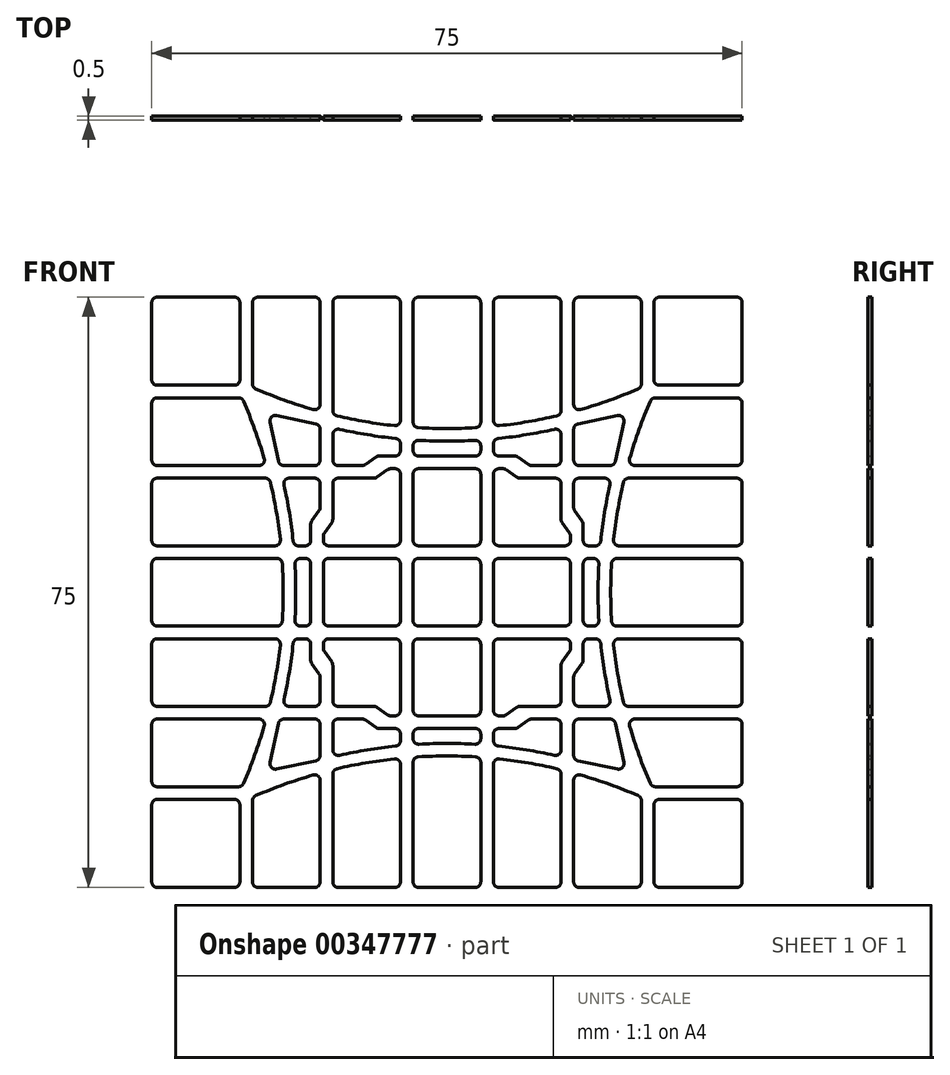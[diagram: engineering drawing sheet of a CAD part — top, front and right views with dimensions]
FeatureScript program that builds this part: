
annotation { "Feature Type Name" : "Feature", "Feature Type Description" : "" }
export const myFeature = defineFeature(function(context is Context, id is Id, definition is map)
    precondition{}
    {
        {
            var Q0;
            Q0=qCreatedBy(makeId("Front.planeOp"),FACE);
            var sketch = newSketch(context, id + "F0", { "sketchPlane" : qUnion([Q0])});
            skLineSegment(sketch, "E0.bottom", {"start": v(39, 39) * mm, "end": v(-39, 39) * mm, "construction": true});
            skLineSegment(sketch, "E0.top", {"start": v(39, -39) * mm, "end": v(-39, -39) * mm, "construction": true});
            skLineSegment(sketch, "E0.left", {"start": v(39, 39) * mm, "end": v(39, -39) * mm, "construction": true});
            skLineSegment(sketch, "E0.right", {"start": v(-39, 39) * mm, "end": v(-39, -39) * mm, "construction": true});
            skPoint(sketch, "E0.middle", {"position": v(0, 0) * mm});
            skLineSegment(sketch, "E1", {"start": v(-39, -25.5) * mm, "end": v(39, -25.5) * mm, "construction": true});
            skLineSegment(sketch, "E2", {"start": v(-39, -39) * mm, "end": v(0, 0) * mm, "construction": true});
            skLineSegment(sketch, "E3", {"start": v(39, -39) * mm, "end": v(0, 0) * mm, "construction": true});
            skPoint(sketch, "E4", {"position": v(-25.5, -25.5) * mm});
            skPoint(sketch, "E5", {"position": v(25.5, -25.5) * mm});
            skLineSegment(sketch, "E6", {"start": v(0, 0) * mm, "end": v(0, -39) * mm, "construction": true});
            skArc(sketch, "E7", {"start": v(25.5, -25.5) * mm, "mid": v(0, -20) * mm, "end": v(-25.5, -25.5) * mm, "construction": true});
            skLineSegment(sketch, "E8", {"start": v(-25.5, -25.5) * mm, "end": v(-25.5, -39) * mm, "construction": true});
            skLineSegment(sketch, "E9", {"start": v(-15.3, -25.5) * mm, "end": v(-15.3, -39) * mm, "construction": true});
            skLineSegment(sketch, "E10", {"start": v(-5.1, -25.5) * mm, "end": v(-5.1, -39) * mm, "construction": true});
            skLineSegment(sketch, "E11.MirrorCS", {"start": v(5.1, -25.5) * mm, "end": v(5.1, -39) * mm, "construction": true});
            skLineSegment(sketch, "E12.MirrorCS", {"start": v(15.3, -25.5) * mm, "end": v(15.3, -39) * mm, "construction": true});
            skLineSegment(sketch, "E13.MirrorCS", {"start": v(25.5, -25.5) * mm, "end": v(25.5, -39) * mm, "construction": true});
            skLineSegment(sketch, "E14", {"start": v(-15.3, -25.5) * mm, "end": v(-15.3, -21.92) * mm, "construction": true});
            skLineSegment(sketch, "E15", {"start": v(-5.1, -25.5) * mm, "end": v(-5.1, -20.21) * mm, "construction": true});
            skLineSegment(sketch, "E16.MirrorCS", {"start": v(5.1, -25.5) * mm, "end": v(5.1, -20.21) * mm, "construction": true});
            skLineSegment(sketch, "E17.MirrorCS", {"start": v(15.3, -25.5) * mm, "end": v(15.3, -21.92) * mm, "construction": true});
            skLineSegment(sketch, "E18", {"start": v(-15.3, -21.92) * mm, "end": v(-15.3, -15.3) * mm, "construction": true});
            skLineSegment(sketch, "E19", {"start": v(-5.1, -20.21) * mm, "end": v(-5.1, -5.1) * mm, "construction": true});
            skLineSegment(sketch, "E20", {"start": v(5.1, -20.21) * mm, "end": v(5.1, -5.1) * mm, "construction": true});
            skLineSegment(sketch, "E21", {"start": v(5.1, -5.1) * mm, "end": v(-5.1, -5.1) * mm, "construction": true});
            skLineSegment(sketch, "E22", {"start": v(-5.1, -16.5) * mm, "end": v(5.1, -16.5) * mm, "construction": true});
            skLineSegment(sketch, "E23", {"start": v(-15.3, -15.3) * mm, "end": v(-9.3, -15.3) * mm, "construction": true});
            skLineSegment(sketch, "E24", {"start": v(-9.3, -15.3) * mm, "end": v(-7.6, -16.5) * mm, "construction": true});
            skLineSegment(sketch, "E25", {"start": v(-7.6, -16.5) * mm, "end": v(-5.1, -16.5) * mm, "construction": true});
            skLineSegment(sketch, "E26", {"start": v(-10.3, -15.3) * mm, "end": v(-8.6, -16.5) * mm, "construction": true});
            skLineSegment(sketch, "E27", {"start": v(-8.6, -16.5) * mm, "end": v(-7.6, -16.5) * mm, "construction": true});
            skArc(sketch, "E28.MirrorCS", {"start": v(-25.5, 25.5) * mm, "mid": v(-20, 0) * mm, "end": v(-25.5, -25.5) * mm, "construction": true});
            skLineSegment(sketch, "E29.MirrorCS", {"start": v(-15.3, -15.3) * mm, "end": v(-15.3, -9.3) * mm, "construction": true});
            skLineSegment(sketch, "E30.MirrorCS", {"start": v(-15.3, -10.3) * mm, "end": v(-16.5, -8.6) * mm, "construction": true});
            skLineSegment(sketch, "E31.MirrorCS", {"start": v(-15.3, -9.3) * mm, "end": v(-16.5, -7.6) * mm, "construction": true});
            skLineSegment(sketch, "E32.MirrorCS", {"start": v(-16.5, -8.6) * mm, "end": v(-16.5, -7.6) * mm, "construction": true});
            skLineSegment(sketch, "E33.MirrorCS", {"start": v(-16.5, -7.6) * mm, "end": v(-16.5, -5.1) * mm, "construction": true});
            skLineSegment(sketch, "E34.MirrorCS", {"start": v(-20.21, -5.1) * mm, "end": v(-5.1, -5.1) * mm, "construction": true});
            skLineSegment(sketch, "E35.MirrorCS", {"start": v(-21.92, -15.3) * mm, "end": v(-15.3, -15.3) * mm, "construction": true});
            skLineSegment(sketch, "E36", {"start": v(-21.92, -15.3) * mm, "end": v(-23.73, -23.73) * mm, "construction": true});
            skLineSegment(sketch, "E37", {"start": v(-23.73, -23.73) * mm, "end": v(-15.3, -21.92) * mm, "construction": true});
            skLineSegment(sketch, "E38.bottom", {"start": v(-3.6, -4.3) * mm, "end": v(3.6, -4.3) * mm});
            skLineSegment(sketch, "E38.top", {"start": v(-3.6, 4.3) * mm, "end": v(3.6, 4.3) * mm});
            skLineSegment(sketch, "E38.left", {"start": v(-4.3, -3.6) * mm, "end": v(-4.3, 3.6) * mm});
            skLineSegment(sketch, "E38.right", {"start": v(4.3, -3.6) * mm, "end": v(4.3, 3.6) * mm});
            skLineSegment(sketch, "E39.bottom", {"start": v(-3.6, -5.9) * mm, "end": v(3.6, -5.9) * mm});
            skLineSegment(sketch, "E39.top", {"start": v(-3.6, -15.7) * mm, "end": v(3.6, -15.7) * mm});
            skLineSegment(sketch, "E39.left", {"start": v(-4.3, -6.6) * mm, "end": v(-4.3, -15) * mm});
            skLineSegment(sketch, "E39.right", {"start": v(4.3, -6.6) * mm, "end": v(4.3, -15) * mm});
            skLineSegment(sketch, "E40.bottom", {"start": v(-36.8, -26.3) * mm, "end": v(-27, -26.3) * mm});
            skLineSegment(sketch, "E40.top", {"start": v(-36.8, -37.5) * mm, "end": v(-27, -37.5) * mm});
            skLineSegment(sketch, "E40.left", {"start": v(-37.5, -27) * mm, "end": v(-37.5, -36.8) * mm});
            skLineSegment(sketch, "E40.right", {"start": v(-26.3, -27) * mm, "end": v(-26.3, -36.8) * mm});
            skArc(sketch, "E41.0", {"start": v(25.83, -24.77) * mm, "mid": v(0, -19.2) * mm, "end": v(-25.83, -24.77) * mm, "construction": true});
            skArc(sketch, "E42.0", {"start": v(25.17, -26.23) * mm, "mid": v(0, -20.8) * mm, "end": v(-25.17, -26.23) * mm, "construction": true});
            skLineSegment(sketch, "E43", {"start": v(-4.3, -18.6) * mm, "end": v(-4.3, -18) * mm});
            skLineSegment(sketch, "E44", {"start": v(-3.6, -17.3) * mm, "end": v(3.6, -17.3) * mm});
            skLineSegment(sketch, "E45", {"start": v(4.3, -18) * mm, "end": v(4.3, -18.6) * mm});
            skArc(sketch, "E46", {"start": v(3.56, -19.3) * mm, "mid": v(0, -19.2) * mm, "end": v(-3.56, -19.3) * mm});
            skLineSegment(sketch, "E47", {"start": v(-4.3, -21.6) * mm, "end": v(-4.3, -36.8) * mm});
            skLineSegment(sketch, "E48", {"start": v(-3.6, -37.5) * mm, "end": v(3.6, -37.5) * mm});
            skLineSegment(sketch, "E49", {"start": v(4.3, -36.8) * mm, "end": v(4.3, -21.6) * mm});
            skArc(sketch, "E50", {"start": v(3.64, -20.9) * mm, "mid": v(0, -20.8) * mm, "end": v(-3.64, -20.9) * mm});
            skLineSegment(sketch, "E51", {"start": v(-24.7, -26.48) * mm, "end": v(-24.7, -36.8) * mm});
            skLineSegment(sketch, "E52", {"start": v(-24, -37.5) * mm, "end": v(-16.8, -37.5) * mm});
            skLineSegment(sketch, "E53", {"start": v(-16.1, -36.8) * mm, "end": v(-16.1, -23.88) * mm});
            skArc(sketch, "E54", {"start": v(-17, -23.21) * mm, "mid": v(-20.68, -24.4) * mm, "end": v(-24.28, -25.83) * mm});
            skLineSegment(sketch, "E55", {"start": v(-14.5, -23.1) * mm, "end": v(-14.5, -36.8) * mm});
            skLineSegment(sketch, "E56", {"start": v(-13.8, -37.5) * mm, "end": v(-6.6, -37.5) * mm});
            skLineSegment(sketch, "E57", {"start": v(-5.9, -36.8) * mm, "end": v(-5.9, -21.86) * mm});
            skArc(sketch, "E58", {"start": v(-6.68, -21.17) * mm, "mid": v(-10.34, -21.68) * mm, "end": v(-13.96, -22.42) * mm});
            skLineSegment(sketch, "E59", {"start": v(-16.1, -16.8) * mm, "end": v(-16.1, -20.7) * mm});
            skLineSegment(sketch, "E60", {"start": v(-16.65, -21.4) * mm, "end": v(-21.63, -22.46) * mm});
            skLineSegment(sketch, "E61.MirrorCS", {"start": v(-21.4, -16.65) * mm, "end": v(-22.46, -21.63) * mm});
            skLineSegment(sketch, "E62.MirrorCS", {"start": v(-16.8, -16.1) * mm, "end": v(-20.7, -16.1) * mm});
            skLineSegment(sketch, "E63", {"start": v(-14.5, -20.02) * mm, "end": v(-14.5, -16.8) * mm});
            skLineSegment(sketch, "E64", {"start": v(-13.8, -16.1) * mm, "end": v(-10.78, -16.1) * mm});
            skLineSegment(sketch, "E65", {"start": v(-10.37, -16.23) * mm, "end": v(-9.04, -17.17) * mm});
            skLineSegment(sketch, "E66", {"start": v(-8.63, -17.3) * mm, "end": v(-6.6, -17.3) * mm});
            skLineSegment(sketch, "E67", {"start": v(-5.9, -18) * mm, "end": v(-5.9, -18.84) * mm});
            skArc(sketch, "E68", {"start": v(-6.53, -19.54) * mm, "mid": v(-10.1, -20.02) * mm, "end": v(-13.65, -20.7) * mm});
            skLineSegment(sketch, "E69", {"start": v(-5.9, -6.6) * mm, "end": v(-5.9, -15) * mm});
            skLineSegment(sketch, "E70", {"start": v(-6.6, -15.7) * mm, "end": v(-7.12, -15.7) * mm});
            skLineSegment(sketch, "E71", {"start": v(-7.53, -15.57) * mm, "end": v(-8.86, -14.63) * mm});
            skLineSegment(sketch, "E72", {"start": v(-9.27, -14.5) * mm, "end": v(-13.8, -14.5) * mm});
            skLineSegment(sketch, "E73.MirrorCS", {"start": v(-6.6, -5.9) * mm, "end": v(-15, -5.9) * mm});
            skLineSegment(sketch, "E74.MirrorCS", {"start": v(-15.7, -6.6) * mm, "end": v(-15.7, -7.12) * mm});
            skLineSegment(sketch, "E75.MirrorCS", {"start": v(-15.57, -7.53) * mm, "end": v(-14.63, -8.86) * mm});
            skLineSegment(sketch, "E76.MirrorCS", {"start": v(-14.5, -9.27) * mm, "end": v(-14.5, -13.8) * mm});
            skPoint(sketch, "E77.visualSharp", {"position": v(-37.5, -26.3) * mm});
            skArc(sketch, "E77.filletArc", {"start": v(-36.8, -26.3) * mm, "mid": v(-37.3, -26.5) * mm, "end": v(-37.5, -27) * mm});
            skPoint(sketch, "E78.visualSharp", {"position": v(-26.3, -26.3) * mm});
            skArc(sketch, "E78.filletArc", {"start": v(-26.3, -27) * mm, "mid": v(-26.5, -26.5) * mm, "end": v(-27, -26.3) * mm});
            skPoint(sketch, "E79.visualSharp", {"position": v(-26.3, -37.5) * mm});
            skArc(sketch, "E79.filletArc", {"start": v(-27, -37.5) * mm, "mid": v(-26.5, -37.3) * mm, "end": v(-26.3, -36.8) * mm});
            skPoint(sketch, "E80.visualSharp", {"position": v(-37.5, -37.5) * mm});
            skArc(sketch, "E80.filletArc", {"start": v(-37.5, -36.8) * mm, "mid": v(-37.3, -37.3) * mm, "end": v(-36.8, -37.5) * mm});
            skPoint(sketch, "E81.visualSharp", {"position": v(-24.7, -37.5) * mm});
            skArc(sketch, "E81.filletArc", {"start": v(-24.7, -36.8) * mm, "mid": v(-24.5, -37.3) * mm, "end": v(-24, -37.5) * mm});
            skPoint(sketch, "E82.visualSharp", {"position": v(-24.7, -26.02) * mm});
            skArc(sketch, "E82.filletArc", {"start": v(-24.28, -25.83) * mm, "mid": v(-24.59, -26.1) * mm, "end": v(-24.7, -26.48) * mm});
            skPoint(sketch, "E83.visualSharp", {"position": v(-16.1, -22.96) * mm});
            skArc(sketch, "E83.filletArc", {"start": v(-16.1, -23.88) * mm, "mid": v(-16.38, -23.33) * mm, "end": v(-17, -23.21) * mm});
            skPoint(sketch, "E84.visualSharp", {"position": v(-16.1, -37.5) * mm});
            skArc(sketch, "E84.filletArc", {"start": v(-16.8, -37.5) * mm, "mid": v(-16.3, -37.3) * mm, "end": v(-16.1, -36.8) * mm});
            skPoint(sketch, "E85.visualSharp", {"position": v(-14.5, -37.5) * mm});
            skArc(sketch, "E85.filletArc", {"start": v(-14.5, -36.8) * mm, "mid": v(-14.3, -37.3) * mm, "end": v(-13.8, -37.5) * mm});
            skPoint(sketch, "E86.visualSharp", {"position": v(-5.9, -37.5) * mm});
            skArc(sketch, "E86.filletArc", {"start": v(-6.6, -37.5) * mm, "mid": v(-6.1, -37.3) * mm, "end": v(-5.9, -36.8) * mm});
            skPoint(sketch, "E87.visualSharp", {"position": v(-5.9, -21.09) * mm});
            skArc(sketch, "E87.filletArc", {"start": v(-5.9, -21.86) * mm, "mid": v(-6.13, -21.34) * mm, "end": v(-6.68, -21.17) * mm});
            skPoint(sketch, "E88.visualSharp", {"position": v(-14.5, -22.55) * mm});
            skArc(sketch, "E88.filletArc", {"start": v(-13.96, -22.42) * mm, "mid": v(-14.35, -22.66) * mm, "end": v(-14.5, -23.1) * mm});
            skPoint(sketch, "E89.visualSharp", {"position": v(-4.3, -37.5) * mm});
            skArc(sketch, "E89.filletArc", {"start": v(-4.3, -36.8) * mm, "mid": v(-4.1, -37.3) * mm, "end": v(-3.6, -37.5) * mm});
            skPoint(sketch, "E90.visualSharp", {"position": v(4.3, -37.5) * mm});
            skArc(sketch, "E90.filletArc", {"start": v(3.6, -37.5) * mm, "mid": v(4.1, -37.3) * mm, "end": v(4.3, -36.8) * mm});
            skPoint(sketch, "E91.visualSharp", {"position": v(4.3, -20.95) * mm});
            skArc(sketch, "E91.filletArc", {"start": v(4.3, -21.6) * mm, "mid": v(4.1, -21.13) * mm, "end": v(3.64, -20.9) * mm});
            skPoint(sketch, "E92.visualSharp", {"position": v(-4.3, -20.95) * mm});
            skArc(sketch, "E92.filletArc", {"start": v(-3.64, -20.9) * mm, "mid": v(-4.1, -21.13) * mm, "end": v(-4.3, -21.6) * mm});
            skPoint(sketch, "E93.visualSharp", {"position": v(-4.3, -17.3) * mm});
            skArc(sketch, "E93.filletArc", {"start": v(-3.6, -17.3) * mm, "mid": v(-4.1, -17.5) * mm, "end": v(-4.3, -18) * mm});
            skPoint(sketch, "E94.visualSharp", {"position": v(4.3, -17.3) * mm});
            skArc(sketch, "E94.filletArc", {"start": v(4.3, -18) * mm, "mid": v(4.1, -17.5) * mm, "end": v(3.6, -17.3) * mm});
            skPoint(sketch, "E95.visualSharp", {"position": v(-4.3, -19.35) * mm});
            skArc(sketch, "E95.filletArc", {"start": v(-4.3, -18.6) * mm, "mid": v(-4.08, -19.11) * mm, "end": v(-3.56, -19.3) * mm});
            skPoint(sketch, "E96.visualSharp", {"position": v(4.3, -19.35) * mm});
            skArc(sketch, "E96.filletArc", {"start": v(3.56, -19.3) * mm, "mid": v(4.08, -19.11) * mm, "end": v(4.3, -18.6) * mm});
            skPoint(sketch, "E97.visualSharp", {"position": v(-14.5, -16.1) * mm});
            skArc(sketch, "E97.filletArc", {"start": v(-13.8, -16.1) * mm, "mid": v(-14.3, -16.3) * mm, "end": v(-14.5, -16.8) * mm});
            skPoint(sketch, "E98.visualSharp", {"position": v(-10.55, -16.1) * mm});
            skArc(sketch, "E98.filletArc", {"start": v(-10.37, -16.23) * mm, "mid": v(-10.56, -16.13) * mm, "end": v(-10.78, -16.1) * mm});
            skPoint(sketch, "E99.visualSharp", {"position": v(-8.85, -17.3) * mm});
            skArc(sketch, "E99.filletArc", {"start": v(-9.04, -17.17) * mm, "mid": v(-8.84, -17.27) * mm, "end": v(-8.63, -17.3) * mm});
            skPoint(sketch, "E100.visualSharp", {"position": v(-5.9, -17.3) * mm});
            skArc(sketch, "E100.filletArc", {"start": v(-5.9, -18) * mm, "mid": v(-6.1, -17.5) * mm, "end": v(-6.6, -17.3) * mm});
            skPoint(sketch, "E101.visualSharp", {"position": v(-5.9, -19.48) * mm});
            skArc(sketch, "E101.filletArc", {"start": v(-6.53, -19.54) * mm, "mid": v(-6.08, -19.31) * mm, "end": v(-5.9, -18.84) * mm});
            skPoint(sketch, "E102.visualSharp", {"position": v(-14.5, -20.9) * mm});
            skArc(sketch, "E102.filletArc", {"start": v(-14.5, -20.02) * mm, "mid": v(-14.24, -20.57) * mm, "end": v(-13.65, -20.7) * mm});
            skPoint(sketch, "E103.visualSharp", {"position": v(-21.28, -16.1) * mm});
            skArc(sketch, "E103.filletArc", {"start": v(-20.7, -16.1) * mm, "mid": v(-21.15, -16.26) * mm, "end": v(-21.4, -16.65) * mm});
            skPoint(sketch, "E104.visualSharp", {"position": v(-16.1, -16.1) * mm});
            skArc(sketch, "E104.filletArc", {"start": v(-16.1, -16.8) * mm, "mid": v(-16.3, -16.3) * mm, "end": v(-16.8, -16.1) * mm});
            skPoint(sketch, "E105.visualSharp", {"position": v(-16.1, -21.28) * mm});
            skArc(sketch, "E105.filletArc", {"start": v(-16.65, -21.4) * mm, "mid": v(-16.26, -21.15) * mm, "end": v(-16.1, -20.7) * mm});
            skPoint(sketch, "E106.visualSharp", {"position": v(-22.7, -22.7) * mm});
            skArc(sketch, "E106.filletArc", {"start": v(-22.46, -21.63) * mm, "mid": v(-22.27, -22.27) * mm, "end": v(-21.63, -22.46) * mm});
            skPoint(sketch, "E107.visualSharp", {"position": v(-14.5, -14.5) * mm});
            skArc(sketch, "E107.filletArc", {"start": v(-14.5, -13.8) * mm, "mid": v(-14.3, -14.3) * mm, "end": v(-13.8, -14.5) * mm});
            skPoint(sketch, "E108.visualSharp", {"position": v(-9.05, -14.5) * mm});
            skArc(sketch, "E108.filletArc", {"start": v(-8.86, -14.63) * mm, "mid": v(-9.06, -14.53) * mm, "end": v(-9.27, -14.5) * mm});
            skPoint(sketch, "E109.visualSharp", {"position": v(-7.35, -15.7) * mm});
            skArc(sketch, "E109.filletArc", {"start": v(-7.53, -15.57) * mm, "mid": v(-7.34, -15.67) * mm, "end": v(-7.12, -15.7) * mm});
            skPoint(sketch, "E110.visualSharp", {"position": v(-5.9, -15.7) * mm});
            skArc(sketch, "E110.filletArc", {"start": v(-6.6, -15.7) * mm, "mid": v(-6.1, -15.5) * mm, "end": v(-5.9, -15) * mm});
            skPoint(sketch, "E111.visualSharp", {"position": v(-5.9, -5.9) * mm});
            skArc(sketch, "E111.filletArc", {"start": v(-5.9, -6.6) * mm, "mid": v(-6.1, -6.1) * mm, "end": v(-6.6, -5.9) * mm});
            skPoint(sketch, "E112.visualSharp", {"position": v(-15.7, -5.9) * mm});
            skArc(sketch, "E112.filletArc", {"start": v(-15, -5.9) * mm, "mid": v(-15.5, -6.1) * mm, "end": v(-15.7, -6.6) * mm});
            skPoint(sketch, "E113.visualSharp", {"position": v(-14.5, -9.05) * mm});
            skArc(sketch, "E113.filletArc", {"start": v(-14.5, -9.27) * mm, "mid": v(-14.53, -9.06) * mm, "end": v(-14.63, -8.86) * mm});
            skPoint(sketch, "E114.visualSharp", {"position": v(-15.7, -7.35) * mm});
            skArc(sketch, "E114.filletArc", {"start": v(-15.7, -7.12) * mm, "mid": v(-15.67, -7.34) * mm, "end": v(-15.57, -7.53) * mm});
            skPoint(sketch, "E115.visualSharp", {"position": v(-4.3, -5.9) * mm});
            skArc(sketch, "E115.filletArc", {"start": v(-3.6, -5.9) * mm, "mid": v(-4.1, -6.1) * mm, "end": v(-4.3, -6.6) * mm});
            skPoint(sketch, "E116.visualSharp", {"position": v(-4.3, -15.7) * mm});
            skArc(sketch, "E116.filletArc", {"start": v(-4.3, -15) * mm, "mid": v(-4.1, -15.5) * mm, "end": v(-3.6, -15.7) * mm});
            skPoint(sketch, "E117.visualSharp", {"position": v(4.3, -15.7) * mm});
            skArc(sketch, "E117.filletArc", {"start": v(3.6, -15.7) * mm, "mid": v(4.1, -15.5) * mm, "end": v(4.3, -15) * mm});
            skPoint(sketch, "E118.visualSharp", {"position": v(4.3, -5.9) * mm});
            skArc(sketch, "E118.filletArc", {"start": v(4.3, -6.6) * mm, "mid": v(4.1, -6.1) * mm, "end": v(3.6, -5.9) * mm});
            skPoint(sketch, "E119.visualSharp", {"position": v(-4.3, 4.3) * mm});
            skArc(sketch, "E119.filletArc", {"start": v(-3.6, 4.3) * mm, "mid": v(-4.1, 4.1) * mm, "end": v(-4.3, 3.6) * mm});
            skPoint(sketch, "E120.visualSharp", {"position": v(-4.3, -4.3) * mm});
            skArc(sketch, "E120.filletArc", {"start": v(-4.3, -3.6) * mm, "mid": v(-4.1, -4.1) * mm, "end": v(-3.6, -4.3) * mm});
            skPoint(sketch, "E121.visualSharp", {"position": v(4.3, -4.3) * mm});
            skArc(sketch, "E121.filletArc", {"start": v(3.6, -4.3) * mm, "mid": v(4.1, -4.1) * mm, "end": v(4.3, -3.6) * mm});
            skPoint(sketch, "E122.visualSharp", {"position": v(4.3, 4.3) * mm});
            skArc(sketch, "E122.filletArc", {"start": v(4.3, 3.6) * mm, "mid": v(4.1, 4.1) * mm, "end": v(3.6, 4.3) * mm});
            skLineSegment(sketch, "E123.MirrorCS", {"start": v(8.63, -17.3) * mm, "end": v(6.6, -17.3) * mm});
            skArc(sketch, "E124.MirrorCS", {"start": v(5.9, -18) * mm, "mid": v(6.1, -17.5) * mm, "end": v(6.6, -17.3) * mm});
            skLineSegment(sketch, "E125.MirrorCS", {"start": v(5.9, -18) * mm, "end": v(5.9, -18.84) * mm});
            skArc(sketch, "E126.MirrorCS", {"start": v(6.53, -19.54) * mm, "mid": v(6.08, -19.31) * mm, "end": v(5.9, -18.84) * mm});
            skArc(sketch, "E127.MirrorCS", {"start": v(6.53, -19.54) * mm, "mid": v(10.1, -20.02) * mm, "end": v(13.65, -20.7) * mm});
            skArc(sketch, "E128.MirrorCS", {"start": v(14.5, -20.02) * mm, "mid": v(14.24, -20.57) * mm, "end": v(13.65, -20.7) * mm});
            skLineSegment(sketch, "E129.MirrorCS", {"start": v(14.5, -20.02) * mm, "end": v(14.5, -16.8) * mm});
            skArc(sketch, "E130.MirrorCS", {"start": v(13.8, -16.1) * mm, "mid": v(14.3, -16.3) * mm, "end": v(14.5, -16.8) * mm});
            skLineSegment(sketch, "E131.MirrorCS", {"start": v(13.8, -16.1) * mm, "end": v(10.78, -16.1) * mm});
            skArc(sketch, "E132.MirrorCS", {"start": v(10.37, -16.23) * mm, "mid": v(10.56, -16.13) * mm, "end": v(10.78, -16.1) * mm});
            skLineSegment(sketch, "E133.MirrorCS", {"start": v(10.37, -16.23) * mm, "end": v(9.04, -17.17) * mm});
            skArc(sketch, "E134.MirrorCS", {"start": v(9.04, -17.17) * mm, "mid": v(8.84, -17.27) * mm, "end": v(8.63, -17.3) * mm});
            skLineSegment(sketch, "E135.MirrorCS", {"start": v(5.9, -36.8) * mm, "end": v(5.9, -21.86) * mm});
            skArc(sketch, "E136.MirrorCS", {"start": v(5.9, -21.86) * mm, "mid": v(6.13, -21.34) * mm, "end": v(6.68, -21.17) * mm});
            skArc(sketch, "E137.MirrorCS", {"start": v(6.6, -37.5) * mm, "mid": v(6.1, -37.3) * mm, "end": v(5.9, -36.8) * mm});
            skLineSegment(sketch, "E138.MirrorCS", {"start": v(13.8, -37.5) * mm, "end": v(6.6, -37.5) * mm});
            skArc(sketch, "E139.MirrorCS", {"start": v(14.5, -36.8) * mm, "mid": v(14.3, -37.3) * mm, "end": v(13.8, -37.5) * mm});
            skLineSegment(sketch, "E140.MirrorCS", {"start": v(14.5, -23.1) * mm, "end": v(14.5, -36.8) * mm});
            skArc(sketch, "E141.MirrorCS", {"start": v(13.96, -22.42) * mm, "mid": v(14.35, -22.66) * mm, "end": v(14.5, -23.1) * mm});
            skArc(sketch, "E142.MirrorCS", {"start": v(6.68, -21.17) * mm, "mid": v(10.34, -21.68) * mm, "end": v(13.96, -22.42) * mm});
            skLineSegment(sketch, "E143.MirrorCS", {"start": v(24.7, -26.48) * mm, "end": v(24.7, -36.8) * mm});
            skArc(sketch, "E144.MirrorCS", {"start": v(24.7, -36.8) * mm, "mid": v(24.5, -37.3) * mm, "end": v(24, -37.5) * mm});
            skLineSegment(sketch, "E145.MirrorCS", {"start": v(24, -37.5) * mm, "end": v(16.8, -37.5) * mm});
            skArc(sketch, "E146.MirrorCS", {"start": v(16.8, -37.5) * mm, "mid": v(16.3, -37.3) * mm, "end": v(16.1, -36.8) * mm});
            skLineSegment(sketch, "E147.MirrorCS", {"start": v(16.1, -36.8) * mm, "end": v(16.1, -23.88) * mm});
            skArc(sketch, "E148.MirrorCS", {"start": v(16.1, -23.88) * mm, "mid": v(16.38, -23.33) * mm, "end": v(17, -23.21) * mm});
            skArc(sketch, "E149.MirrorCS", {"start": v(24.28, -25.83) * mm, "mid": v(24.59, -26.1) * mm, "end": v(24.7, -26.48) * mm});
            skArc(sketch, "E150.MirrorCS", {"start": v(17, -23.21) * mm, "mid": v(20.68, -24.4) * mm, "end": v(24.28, -25.83) * mm});
            skPoint(sketch, "E151.1.0", {"position": v(37.5, -37.5) * mm});
            skPoint(sketch, "E151.1.1", {"position": v(37.5, -26.3) * mm});
            skLineSegment(sketch, "E151.1.3", {"start": v(26.3, -36.8) * mm, "end": v(26.3, -27) * mm});
            skPoint(sketch, "E151.1.4", {"position": v(26.3, -37.5) * mm});
            skLineSegment(sketch, "E151.1.5", {"start": v(37.5, -36.8) * mm, "end": v(37.5, -27) * mm});
            skLineSegment(sketch, "E151.1.6", {"start": v(27, -26.3) * mm, "end": v(36.8, -26.3) * mm});
            skPoint(sketch, "E151.1.7", {"position": v(26.3, -26.3) * mm});
            skLineSegment(sketch, "E151.1.8", {"start": v(27, -37.5) * mm, "end": v(36.8, -37.5) * mm});
            skArc(sketch, "E151.1.9", {"start": v(26.3, -36.8) * mm, "mid": v(26.5, -37.3) * mm, "end": v(27, -37.5) * mm});
            skArc(sketch, "E151.1.10", {"start": v(36.8, -37.5) * mm, "mid": v(37.3, -37.3) * mm, "end": v(37.5, -36.8) * mm});
            skArc(sketch, "E151.1.11", {"start": v(27, -26.3) * mm, "mid": v(26.5, -26.5) * mm, "end": v(26.3, -27) * mm});
            skArc(sketch, "E151.1.12", {"start": v(37.5, -27) * mm, "mid": v(37.3, -26.5) * mm, "end": v(36.8, -26.3) * mm});
            skPoint(sketch, "E151.2.0", {"position": v(37.5, 37.5) * mm});
            skPoint(sketch, "E151.2.1", {"position": v(26.3, 37.5) * mm});
            skPoint(sketch, "E151.2.2", {"position": v(25.5, 25.5) * mm});
            skLineSegment(sketch, "E151.2.3", {"start": v(36.8, 26.3) * mm, "end": v(27, 26.3) * mm});
            skPoint(sketch, "E151.2.4", {"position": v(37.5, 26.3) * mm});
            skLineSegment(sketch, "E151.2.5", {"start": v(36.8, 37.5) * mm, "end": v(27, 37.5) * mm});
            skLineSegment(sketch, "E151.2.6", {"start": v(26.3, 27) * mm, "end": v(26.3, 36.8) * mm});
            skPoint(sketch, "E151.2.7", {"position": v(26.3, 26.3) * mm});
            skLineSegment(sketch, "E151.2.8", {"start": v(37.5, 27) * mm, "end": v(37.5, 36.8) * mm});
            skArc(sketch, "E151.2.9", {"start": v(36.8, 26.3) * mm, "mid": v(37.3, 26.5) * mm, "end": v(37.5, 27) * mm});
            skArc(sketch, "E151.2.10", {"start": v(37.5, 36.8) * mm, "mid": v(37.3, 37.3) * mm, "end": v(36.8, 37.5) * mm});
            skArc(sketch, "E151.2.11", {"start": v(26.3, 27) * mm, "mid": v(26.5, 26.5) * mm, "end": v(27, 26.3) * mm});
            skArc(sketch, "E151.2.12", {"start": v(27, 37.5) * mm, "mid": v(26.5, 37.3) * mm, "end": v(26.3, 36.8) * mm});
            skPoint(sketch, "E151.3.0", {"position": v(-37.5, 37.5) * mm});
            skPoint(sketch, "E151.3.1", {"position": v(-37.5, 26.3) * mm});
            skPoint(sketch, "E151.3.2", {"position": v(-25.5, 25.5) * mm});
            skLineSegment(sketch, "E151.3.3", {"start": v(-26.3, 36.8) * mm, "end": v(-26.3, 27) * mm});
            skPoint(sketch, "E151.3.4", {"position": v(-26.3, 37.5) * mm});
            skLineSegment(sketch, "E151.3.5", {"start": v(-37.5, 36.8) * mm, "end": v(-37.5, 27) * mm});
            skLineSegment(sketch, "E151.3.6", {"start": v(-27, 26.3) * mm, "end": v(-36.8, 26.3) * mm});
            skPoint(sketch, "E151.3.7", {"position": v(-26.3, 26.3) * mm});
            skLineSegment(sketch, "E151.3.8", {"start": v(-27, 37.5) * mm, "end": v(-36.8, 37.5) * mm});
            skArc(sketch, "E151.3.9", {"start": v(-26.3, 36.8) * mm, "mid": v(-26.5, 37.3) * mm, "end": v(-27, 37.5) * mm});
            skArc(sketch, "E151.3.10", {"start": v(-36.8, 37.5) * mm, "mid": v(-37.3, 37.3) * mm, "end": v(-37.5, 36.8) * mm});
            skArc(sketch, "E151.3.11", {"start": v(-27, 26.3) * mm, "mid": v(-26.5, 26.5) * mm, "end": v(-26.3, 27) * mm});
            skArc(sketch, "E151.3.12", {"start": v(-37.5, 27) * mm, "mid": v(-37.3, 26.5) * mm, "end": v(-36.8, 26.3) * mm});
            skLineSegment(sketch, "E152.1.0", {"start": v(37.5, -24) * mm, "end": v(37.5, -16.8) * mm});
            skArc(sketch, "E152.1.1", {"start": v(37.5, -16.8) * mm, "mid": v(37.3, -16.3) * mm, "end": v(36.8, -16.1) * mm});
            skArc(sketch, "E152.1.2", {"start": v(36.8, -24.7) * mm, "mid": v(37.3, -24.5) * mm, "end": v(37.5, -24) * mm});
            skLineSegment(sketch, "E152.1.3", {"start": v(26.48, -24.7) * mm, "end": v(36.8, -24.7) * mm});
            skLineSegment(sketch, "E152.1.4", {"start": v(36.8, -16.1) * mm, "end": v(23.88, -16.1) * mm});
            skArc(sketch, "E152.1.5", {"start": v(25.83, -24.28) * mm, "mid": v(26.1, -24.59) * mm, "end": v(26.48, -24.7) * mm});
            skArc(sketch, "E152.1.6", {"start": v(23.88, -16.1) * mm, "mid": v(23.33, -16.38) * mm, "end": v(23.21, -17) * mm});
            skArc(sketch, "E152.1.7", {"start": v(23.21, -17) * mm, "mid": v(24.4, -20.68) * mm, "end": v(25.83, -24.28) * mm});
            skArc(sketch, "E152.1.8", {"start": v(22.42, -13.96) * mm, "mid": v(22.66, -14.35) * mm, "end": v(23.1, -14.5) * mm});
            skLineSegment(sketch, "E152.1.9", {"start": v(23.1, -14.5) * mm, "end": v(36.8, -14.5) * mm});
            skArc(sketch, "E152.1.10", {"start": v(21.17, -6.68) * mm, "mid": v(21.68, -10.34) * mm, "end": v(22.42, -13.96) * mm});
            skArc(sketch, "E152.1.11", {"start": v(21.86, -5.9) * mm, "mid": v(21.34, -6.13) * mm, "end": v(21.17, -6.68) * mm});
            skLineSegment(sketch, "E152.1.12", {"start": v(36.8, -5.9) * mm, "end": v(21.86, -5.9) * mm});
            skArc(sketch, "E152.1.13", {"start": v(36.8, -14.5) * mm, "mid": v(37.3, -14.3) * mm, "end": v(37.5, -13.8) * mm});
            skLineSegment(sketch, "E152.1.14", {"start": v(37.5, -13.8) * mm, "end": v(37.5, -6.6) * mm});
            skArc(sketch, "E152.1.15", {"start": v(37.5, -6.6) * mm, "mid": v(37.3, -6.1) * mm, "end": v(36.8, -5.9) * mm});
            skLineSegment(sketch, "E152.1.16", {"start": v(37.5, -3.6) * mm, "end": v(37.5, 3.6) * mm});
            skArc(sketch, "E152.1.17", {"start": v(36.8, -4.3) * mm, "mid": v(37.3, -4.1) * mm, "end": v(37.5, -3.6) * mm});
            skArc(sketch, "E152.1.18", {"start": v(37.5, 3.6) * mm, "mid": v(37.3, 4.1) * mm, "end": v(36.8, 4.3) * mm});
            skLineSegment(sketch, "E152.1.19", {"start": v(36.8, 4.3) * mm, "end": v(21.6, 4.3) * mm});
            skLineSegment(sketch, "E152.1.20", {"start": v(21.6, -4.3) * mm, "end": v(36.8, -4.3) * mm});
            skArc(sketch, "E152.1.21", {"start": v(20.9, -3.64) * mm, "mid": v(21.13, -4.1) * mm, "end": v(21.6, -4.3) * mm});
            skArc(sketch, "E152.1.22", {"start": v(20.9, 3.64) * mm, "mid": v(20.8, 0) * mm, "end": v(20.9, -3.64) * mm});
            skArc(sketch, "E152.1.23", {"start": v(21.6, 4.3) * mm, "mid": v(21.13, 4.1) * mm, "end": v(20.9, 3.64) * mm});
            skLineSegment(sketch, "E152.1.24", {"start": v(36.8, 5.9) * mm, "end": v(21.86, 5.9) * mm});
            skArc(sketch, "E152.1.25", {"start": v(37.5, 6.6) * mm, "mid": v(37.3, 6.1) * mm, "end": v(36.8, 5.9) * mm});
            skLineSegment(sketch, "E152.1.26", {"start": v(37.5, 13.8) * mm, "end": v(37.5, 6.6) * mm});
            skArc(sketch, "E152.1.27", {"start": v(36.8, 14.5) * mm, "mid": v(37.3, 14.3) * mm, "end": v(37.5, 13.8) * mm});
            skLineSegment(sketch, "E152.1.28", {"start": v(23.1, 14.5) * mm, "end": v(36.8, 14.5) * mm});
            skArc(sketch, "E152.1.29", {"start": v(22.42, 13.96) * mm, "mid": v(22.66, 14.35) * mm, "end": v(23.1, 14.5) * mm});
            skArc(sketch, "E152.1.30", {"start": v(21.17, 6.68) * mm, "mid": v(21.68, 10.34) * mm, "end": v(22.42, 13.96) * mm});
            skArc(sketch, "E152.1.31", {"start": v(21.86, 5.9) * mm, "mid": v(21.34, 6.13) * mm, "end": v(21.17, 6.68) * mm});
            skLineSegment(sketch, "E152.1.32", {"start": v(36.8, 16.1) * mm, "end": v(23.88, 16.1) * mm});
            skArc(sketch, "E152.1.33", {"start": v(23.88, 16.1) * mm, "mid": v(23.33, 16.38) * mm, "end": v(23.21, 17) * mm});
            skArc(sketch, "E152.1.34", {"start": v(23.21, 17) * mm, "mid": v(24.4, 20.68) * mm, "end": v(25.83, 24.28) * mm});
            skArc(sketch, "E152.1.35", {"start": v(25.83, 24.28) * mm, "mid": v(26.1, 24.59) * mm, "end": v(26.48, 24.7) * mm});
            skLineSegment(sketch, "E152.1.36", {"start": v(26.48, 24.7) * mm, "end": v(36.8, 24.7) * mm});
            skArc(sketch, "E152.1.37", {"start": v(36.8, 24.7) * mm, "mid": v(37.3, 24.5) * mm, "end": v(37.5, 24) * mm});
            skLineSegment(sketch, "E152.1.38", {"start": v(37.5, 24) * mm, "end": v(37.5, 16.8) * mm});
            skArc(sketch, "E152.1.39", {"start": v(37.5, 16.8) * mm, "mid": v(37.3, 16.3) * mm, "end": v(36.8, 16.1) * mm});
            skLineSegment(sketch, "E152.2.0", {"start": v(24, 37.5) * mm, "end": v(16.8, 37.5) * mm});
            skArc(sketch, "E152.2.1", {"start": v(16.8, 37.5) * mm, "mid": v(16.3, 37.3) * mm, "end": v(16.1, 36.8) * mm});
            skArc(sketch, "E152.2.2", {"start": v(24.7, 36.8) * mm, "mid": v(24.5, 37.3) * mm, "end": v(24, 37.5) * mm});
            skLineSegment(sketch, "E152.2.3", {"start": v(24.7, 26.48) * mm, "end": v(24.7, 36.8) * mm});
            skLineSegment(sketch, "E152.2.4", {"start": v(16.1, 36.8) * mm, "end": v(16.1, 23.88) * mm});
            skArc(sketch, "E152.2.5", {"start": v(24.28, 25.83) * mm, "mid": v(24.59, 26.1) * mm, "end": v(24.7, 26.48) * mm});
            skArc(sketch, "E152.2.6", {"start": v(16.1, 23.88) * mm, "mid": v(16.38, 23.33) * mm, "end": v(17, 23.21) * mm});
            skArc(sketch, "E152.2.7", {"start": v(17, 23.21) * mm, "mid": v(20.68, 24.4) * mm, "end": v(24.28, 25.83) * mm});
            skArc(sketch, "E152.2.8", {"start": v(13.96, 22.42) * mm, "mid": v(14.35, 22.66) * mm, "end": v(14.5, 23.1) * mm});
            skLineSegment(sketch, "E152.2.9", {"start": v(14.5, 23.1) * mm, "end": v(14.5, 36.8) * mm});
            skArc(sketch, "E152.2.10", {"start": v(6.68, 21.17) * mm, "mid": v(10.34, 21.68) * mm, "end": v(13.96, 22.42) * mm});
            skArc(sketch, "E152.2.11", {"start": v(5.9, 21.86) * mm, "mid": v(6.13, 21.34) * mm, "end": v(6.68, 21.17) * mm});
            skLineSegment(sketch, "E152.2.12", {"start": v(5.9, 36.8) * mm, "end": v(5.9, 21.86) * mm});
            skArc(sketch, "E152.2.13", {"start": v(14.5, 36.8) * mm, "mid": v(14.3, 37.3) * mm, "end": v(13.8, 37.5) * mm});
            skLineSegment(sketch, "E152.2.14", {"start": v(13.8, 37.5) * mm, "end": v(6.6, 37.5) * mm});
            skArc(sketch, "E152.2.15", {"start": v(6.6, 37.5) * mm, "mid": v(6.1, 37.3) * mm, "end": v(5.9, 36.8) * mm});
            skLineSegment(sketch, "E152.2.16", {"start": v(3.6, 37.5) * mm, "end": v(-3.6, 37.5) * mm});
            skArc(sketch, "E152.2.17", {"start": v(4.3, 36.8) * mm, "mid": v(4.1, 37.3) * mm, "end": v(3.6, 37.5) * mm});
            skArc(sketch, "E152.2.18", {"start": v(-3.6, 37.5) * mm, "mid": v(-4.1, 37.3) * mm, "end": v(-4.3, 36.8) * mm});
            skLineSegment(sketch, "E152.2.19", {"start": v(-4.3, 36.8) * mm, "end": v(-4.3, 21.6) * mm});
            skLineSegment(sketch, "E152.2.20", {"start": v(4.3, 21.6) * mm, "end": v(4.3, 36.8) * mm});
            skArc(sketch, "E152.2.21", {"start": v(3.64, 20.9) * mm, "mid": v(4.1, 21.13) * mm, "end": v(4.3, 21.6) * mm});
            skArc(sketch, "E152.2.22", {"start": v(-3.64, 20.9) * mm, "mid": v(0, 20.8) * mm, "end": v(3.64, 20.9) * mm});
            skArc(sketch, "E152.2.23", {"start": v(-4.3, 21.6) * mm, "mid": v(-4.1, 21.13) * mm, "end": v(-3.64, 20.9) * mm});
            skLineSegment(sketch, "E152.2.24", {"start": v(-5.9, 36.8) * mm, "end": v(-5.9, 21.86) * mm});
            skArc(sketch, "E152.2.25", {"start": v(-6.6, 37.5) * mm, "mid": v(-6.1, 37.3) * mm, "end": v(-5.9, 36.8) * mm});
            skLineSegment(sketch, "E152.2.26", {"start": v(-13.8, 37.5) * mm, "end": v(-6.6, 37.5) * mm});
            skArc(sketch, "E152.2.27", {"start": v(-14.5, 36.8) * mm, "mid": v(-14.3, 37.3) * mm, "end": v(-13.8, 37.5) * mm});
            skLineSegment(sketch, "E152.2.28", {"start": v(-14.5, 23.1) * mm, "end": v(-14.5, 36.8) * mm});
            skArc(sketch, "E152.2.29", {"start": v(-13.96, 22.42) * mm, "mid": v(-14.35, 22.66) * mm, "end": v(-14.5, 23.1) * mm});
            skArc(sketch, "E152.2.30", {"start": v(-6.68, 21.17) * mm, "mid": v(-10.34, 21.68) * mm, "end": v(-13.96, 22.42) * mm});
            skArc(sketch, "E152.2.31", {"start": v(-5.9, 21.86) * mm, "mid": v(-6.13, 21.34) * mm, "end": v(-6.68, 21.17) * mm});
            skLineSegment(sketch, "E152.2.32", {"start": v(-16.1, 36.8) * mm, "end": v(-16.1, 23.88) * mm});
            skArc(sketch, "E152.2.33", {"start": v(-16.1, 23.88) * mm, "mid": v(-16.38, 23.33) * mm, "end": v(-17, 23.21) * mm});
            skArc(sketch, "E152.2.34", {"start": v(-17, 23.21) * mm, "mid": v(-20.68, 24.4) * mm, "end": v(-24.28, 25.83) * mm});
            skArc(sketch, "E152.2.35", {"start": v(-24.28, 25.83) * mm, "mid": v(-24.59, 26.1) * mm, "end": v(-24.7, 26.48) * mm});
            skLineSegment(sketch, "E152.2.36", {"start": v(-24.7, 26.48) * mm, "end": v(-24.7, 36.8) * mm});
            skArc(sketch, "E152.2.37", {"start": v(-24.7, 36.8) * mm, "mid": v(-24.5, 37.3) * mm, "end": v(-24, 37.5) * mm});
            skLineSegment(sketch, "E152.2.38", {"start": v(-24, 37.5) * mm, "end": v(-16.8, 37.5) * mm});
            skArc(sketch, "E152.2.39", {"start": v(-16.8, 37.5) * mm, "mid": v(-16.3, 37.3) * mm, "end": v(-16.1, 36.8) * mm});
            skLineSegment(sketch, "E152.3.0", {"start": v(-37.5, 24) * mm, "end": v(-37.5, 16.8) * mm});
            skArc(sketch, "E152.3.1", {"start": v(-37.5, 16.8) * mm, "mid": v(-37.3, 16.3) * mm, "end": v(-36.8, 16.1) * mm});
            skArc(sketch, "E152.3.2", {"start": v(-36.8, 24.7) * mm, "mid": v(-37.3, 24.5) * mm, "end": v(-37.5, 24) * mm});
            skLineSegment(sketch, "E152.3.3", {"start": v(-26.48, 24.7) * mm, "end": v(-36.8, 24.7) * mm});
            skLineSegment(sketch, "E152.3.4", {"start": v(-36.8, 16.1) * mm, "end": v(-23.88, 16.1) * mm});
            skArc(sketch, "E152.3.5", {"start": v(-25.83, 24.28) * mm, "mid": v(-26.1, 24.59) * mm, "end": v(-26.48, 24.7) * mm});
            skArc(sketch, "E152.3.6", {"start": v(-23.88, 16.1) * mm, "mid": v(-23.33, 16.38) * mm, "end": v(-23.21, 17) * mm});
            skArc(sketch, "E152.3.7", {"start": v(-23.21, 17) * mm, "mid": v(-24.4, 20.68) * mm, "end": v(-25.83, 24.28) * mm});
            skArc(sketch, "E152.3.8", {"start": v(-22.42, 13.96) * mm, "mid": v(-22.66, 14.35) * mm, "end": v(-23.1, 14.5) * mm});
            skLineSegment(sketch, "E152.3.9", {"start": v(-23.1, 14.5) * mm, "end": v(-36.8, 14.5) * mm});
            skArc(sketch, "E152.3.10", {"start": v(-21.17, 6.68) * mm, "mid": v(-21.68, 10.34) * mm, "end": v(-22.42, 13.96) * mm});
            skArc(sketch, "E152.3.11", {"start": v(-21.86, 5.9) * mm, "mid": v(-21.34, 6.13) * mm, "end": v(-21.17, 6.68) * mm});
            skLineSegment(sketch, "E152.3.12", {"start": v(-36.8, 5.9) * mm, "end": v(-21.86, 5.9) * mm});
            skArc(sketch, "E152.3.13", {"start": v(-36.8, 14.5) * mm, "mid": v(-37.3, 14.3) * mm, "end": v(-37.5, 13.8) * mm});
            skLineSegment(sketch, "E152.3.14", {"start": v(-37.5, 13.8) * mm, "end": v(-37.5, 6.6) * mm});
            skArc(sketch, "E152.3.15", {"start": v(-37.5, 6.6) * mm, "mid": v(-37.3, 6.1) * mm, "end": v(-36.8, 5.9) * mm});
            skLineSegment(sketch, "E152.3.16", {"start": v(-37.5, 3.6) * mm, "end": v(-37.5, -3.6) * mm});
            skArc(sketch, "E152.3.17", {"start": v(-36.8, 4.3) * mm, "mid": v(-37.3, 4.1) * mm, "end": v(-37.5, 3.6) * mm});
            skArc(sketch, "E152.3.18", {"start": v(-37.5, -3.6) * mm, "mid": v(-37.3, -4.1) * mm, "end": v(-36.8, -4.3) * mm});
            skLineSegment(sketch, "E152.3.19", {"start": v(-36.8, -4.3) * mm, "end": v(-21.6, -4.3) * mm});
            skLineSegment(sketch, "E152.3.20", {"start": v(-21.6, 4.3) * mm, "end": v(-36.8, 4.3) * mm});
            skArc(sketch, "E152.3.21", {"start": v(-20.9, 3.64) * mm, "mid": v(-21.13, 4.1) * mm, "end": v(-21.6, 4.3) * mm});
            skArc(sketch, "E152.3.22", {"start": v(-20.9, -3.64) * mm, "mid": v(-20.8, 0) * mm, "end": v(-20.9, 3.64) * mm});
            skArc(sketch, "E152.3.23", {"start": v(-21.6, -4.3) * mm, "mid": v(-21.13, -4.1) * mm, "end": v(-20.9, -3.64) * mm});
            skLineSegment(sketch, "E152.3.24", {"start": v(-36.8, -5.9) * mm, "end": v(-21.86, -5.9) * mm});
            skArc(sketch, "E152.3.25", {"start": v(-37.5, -6.6) * mm, "mid": v(-37.3, -6.1) * mm, "end": v(-36.8, -5.9) * mm});
            skLineSegment(sketch, "E152.3.26", {"start": v(-37.5, -13.8) * mm, "end": v(-37.5, -6.6) * mm});
            skArc(sketch, "E152.3.27", {"start": v(-36.8, -14.5) * mm, "mid": v(-37.3, -14.3) * mm, "end": v(-37.5, -13.8) * mm});
            skLineSegment(sketch, "E152.3.28", {"start": v(-23.1, -14.5) * mm, "end": v(-36.8, -14.5) * mm});
            skArc(sketch, "E152.3.29", {"start": v(-22.42, -13.96) * mm, "mid": v(-22.66, -14.35) * mm, "end": v(-23.1, -14.5) * mm});
            skArc(sketch, "E152.3.30", {"start": v(-21.17, -6.68) * mm, "mid": v(-21.68, -10.34) * mm, "end": v(-22.42, -13.96) * mm});
            skArc(sketch, "E152.3.31", {"start": v(-21.86, -5.9) * mm, "mid": v(-21.34, -6.13) * mm, "end": v(-21.17, -6.68) * mm});
            skLineSegment(sketch, "E152.3.32", {"start": v(-36.8, -16.1) * mm, "end": v(-23.88, -16.1) * mm});
            skArc(sketch, "E152.3.33", {"start": v(-23.88, -16.1) * mm, "mid": v(-23.33, -16.38) * mm, "end": v(-23.21, -17) * mm});
            skArc(sketch, "E152.3.34", {"start": v(-23.21, -17) * mm, "mid": v(-24.4, -20.68) * mm, "end": v(-25.83, -24.28) * mm});
            skArc(sketch, "E152.3.35", {"start": v(-25.83, -24.28) * mm, "mid": v(-26.1, -24.59) * mm, "end": v(-26.48, -24.7) * mm});
            skLineSegment(sketch, "E152.3.36", {"start": v(-26.48, -24.7) * mm, "end": v(-36.8, -24.7) * mm});
            skArc(sketch, "E152.3.37", {"start": v(-36.8, -24.7) * mm, "mid": v(-37.3, -24.5) * mm, "end": v(-37.5, -24) * mm});
            skLineSegment(sketch, "E152.3.38", {"start": v(-37.5, -24) * mm, "end": v(-37.5, -16.8) * mm});
            skArc(sketch, "E152.3.39", {"start": v(-37.5, -16.8) * mm, "mid": v(-37.3, -16.3) * mm, "end": v(-36.8, -16.1) * mm});
            skArc(sketch, "E153.1.0", {"start": v(5.9, -3.6) * mm, "mid": v(6.1, -4.1) * mm, "end": v(6.6, -4.3) * mm});
            skLineSegment(sketch, "E153.1.1", {"start": v(6.6, -4.3) * mm, "end": v(15, -4.3) * mm});
            skArc(sketch, "E153.1.2", {"start": v(15, -4.3) * mm, "mid": v(15.5, -4.1) * mm, "end": v(15.7, -3.6) * mm});
            skLineSegment(sketch, "E153.1.3", {"start": v(15.7, -3.6) * mm, "end": v(15.7, 3.6) * mm});
            skArc(sketch, "E153.1.4", {"start": v(15.7, 3.6) * mm, "mid": v(15.5, 4.1) * mm, "end": v(15, 4.3) * mm});
            skLineSegment(sketch, "E153.1.5", {"start": v(6.6, 4.3) * mm, "end": v(15, 4.3) * mm});
            skArc(sketch, "E153.1.6", {"start": v(6.6, 4.3) * mm, "mid": v(6.1, 4.1) * mm, "end": v(5.9, 3.6) * mm});
            skLineSegment(sketch, "E153.1.7", {"start": v(5.9, -3.6) * mm, "end": v(5.9, 3.6) * mm});
            skArc(sketch, "E153.2.0", {"start": v(3.6, 5.9) * mm, "mid": v(4.1, 6.1) * mm, "end": v(4.3, 6.6) * mm});
            skLineSegment(sketch, "E153.2.1", {"start": v(4.3, 6.6) * mm, "end": v(4.3, 15) * mm});
            skArc(sketch, "E153.2.2", {"start": v(4.3, 15) * mm, "mid": v(4.1, 15.5) * mm, "end": v(3.6, 15.7) * mm});
            skLineSegment(sketch, "E153.2.3", {"start": v(3.6, 15.7) * mm, "end": v(-3.6, 15.7) * mm});
            skArc(sketch, "E153.2.4", {"start": v(-3.6, 15.7) * mm, "mid": v(-4.1, 15.5) * mm, "end": v(-4.3, 15) * mm});
            skLineSegment(sketch, "E153.2.5", {"start": v(-4.3, 6.6) * mm, "end": v(-4.3, 15) * mm});
            skArc(sketch, "E153.2.6", {"start": v(-4.3, 6.6) * mm, "mid": v(-4.1, 6.1) * mm, "end": v(-3.6, 5.9) * mm});
            skLineSegment(sketch, "E153.2.7", {"start": v(3.6, 5.9) * mm, "end": v(-3.6, 5.9) * mm});
            skArc(sketch, "E153.3.0", {"start": v(-5.9, 3.6) * mm, "mid": v(-6.1, 4.1) * mm, "end": v(-6.6, 4.3) * mm});
            skLineSegment(sketch, "E153.3.1", {"start": v(-6.6, 4.3) * mm, "end": v(-15, 4.3) * mm});
            skArc(sketch, "E153.3.2", {"start": v(-15, 4.3) * mm, "mid": v(-15.5, 4.1) * mm, "end": v(-15.7, 3.6) * mm});
            skLineSegment(sketch, "E153.3.3", {"start": v(-15.7, 3.6) * mm, "end": v(-15.7, -3.6) * mm});
            skArc(sketch, "E153.3.4", {"start": v(-15.7, -3.6) * mm, "mid": v(-15.5, -4.1) * mm, "end": v(-15, -4.3) * mm});
            skLineSegment(sketch, "E153.3.5", {"start": v(-6.6, -4.3) * mm, "end": v(-15, -4.3) * mm});
            skArc(sketch, "E153.3.6", {"start": v(-6.6, -4.3) * mm, "mid": v(-6.1, -4.1) * mm, "end": v(-5.9, -3.6) * mm});
            skLineSegment(sketch, "E153.3.7", {"start": v(-5.9, 3.6) * mm, "end": v(-5.9, -3.6) * mm});
            skArc(sketch, "E154.1.0", {"start": v(17.3, -3.6) * mm, "mid": v(17.5, -4.1) * mm, "end": v(18, -4.3) * mm});
            skArc(sketch, "E154.1.1", {"start": v(18.6, -4.3) * mm, "mid": v(19.11, -4.08) * mm, "end": v(19.3, -3.56) * mm});
            skLineSegment(sketch, "E154.1.2", {"start": v(18.6, -4.3) * mm, "end": v(18, -4.3) * mm});
            skLineSegment(sketch, "E154.1.3", {"start": v(17.3, -3.6) * mm, "end": v(17.3, 3.6) * mm});
            skArc(sketch, "E154.1.4", {"start": v(19.3, 3.56) * mm, "mid": v(19.2, 0) * mm, "end": v(19.3, -3.56) * mm});
            skArc(sketch, "E154.1.5", {"start": v(19.3, 3.56) * mm, "mid": v(19.11, 4.08) * mm, "end": v(18.6, 4.3) * mm});
            skLineSegment(sketch, "E154.1.6", {"start": v(18, 4.3) * mm, "end": v(18.6, 4.3) * mm});
            skArc(sketch, "E154.1.7", {"start": v(18, 4.3) * mm, "mid": v(17.5, 4.1) * mm, "end": v(17.3, 3.6) * mm});
            skArc(sketch, "E154.2.0", {"start": v(3.6, 17.3) * mm, "mid": v(4.1, 17.5) * mm, "end": v(4.3, 18) * mm});
            skArc(sketch, "E154.2.1", {"start": v(4.3, 18.6) * mm, "mid": v(4.08, 19.11) * mm, "end": v(3.56, 19.3) * mm});
            skLineSegment(sketch, "E154.2.2", {"start": v(4.3, 18.6) * mm, "end": v(4.3, 18) * mm});
            skLineSegment(sketch, "E154.2.3", {"start": v(3.6, 17.3) * mm, "end": v(-3.6, 17.3) * mm});
            skArc(sketch, "E154.2.4", {"start": v(-3.56, 19.3) * mm, "mid": v(0, 19.2) * mm, "end": v(3.56, 19.3) * mm});
            skArc(sketch, "E154.2.5", {"start": v(-3.56, 19.3) * mm, "mid": v(-4.08, 19.11) * mm, "end": v(-4.3, 18.6) * mm});
            skLineSegment(sketch, "E154.2.6", {"start": v(-4.3, 18) * mm, "end": v(-4.3, 18.6) * mm});
            skArc(sketch, "E154.2.7", {"start": v(-4.3, 18) * mm, "mid": v(-4.1, 17.5) * mm, "end": v(-3.6, 17.3) * mm});
            skArc(sketch, "E154.3.0", {"start": v(-17.3, 3.6) * mm, "mid": v(-17.5, 4.1) * mm, "end": v(-18, 4.3) * mm});
            skArc(sketch, "E154.3.1", {"start": v(-18.6, 4.3) * mm, "mid": v(-19.11, 4.08) * mm, "end": v(-19.3, 3.56) * mm});
            skLineSegment(sketch, "E154.3.2", {"start": v(-18.6, 4.3) * mm, "end": v(-18, 4.3) * mm});
            skLineSegment(sketch, "E154.3.3", {"start": v(-17.3, 3.6) * mm, "end": v(-17.3, -3.6) * mm});
            skArc(sketch, "E154.3.4", {"start": v(-19.3, -3.56) * mm, "mid": v(-19.2, 0) * mm, "end": v(-19.3, 3.56) * mm});
            skArc(sketch, "E154.3.5", {"start": v(-19.3, -3.56) * mm, "mid": v(-19.11, -4.08) * mm, "end": v(-18.6, -4.3) * mm});
            skLineSegment(sketch, "E154.3.6", {"start": v(-18, -4.3) * mm, "end": v(-18.6, -4.3) * mm});
            skArc(sketch, "E154.3.7", {"start": v(-18, -4.3) * mm, "mid": v(-17.5, -4.1) * mm, "end": v(-17.3, -3.6) * mm});
            skLineSegment(sketch, "E155.MirrorCS", {"start": v(5.9, -6.6) * mm, "end": v(5.9, -15) * mm});
            skArc(sketch, "E156.MirrorCS", {"start": v(5.9, -6.6) * mm, "mid": v(6.1, -6.1) * mm, "end": v(6.6, -5.9) * mm});
            skLineSegment(sketch, "E157.MirrorCS", {"start": v(6.6, -5.9) * mm, "end": v(15, -5.9) * mm});
            skArc(sketch, "E158.MirrorCS", {"start": v(15, -5.9) * mm, "mid": v(15.5, -6.1) * mm, "end": v(15.7, -6.6) * mm});
            skLineSegment(sketch, "E159.MirrorCS", {"start": v(15.7, -6.6) * mm, "end": v(15.7, -7.12) * mm});
            skArc(sketch, "E160.MirrorCS", {"start": v(15.7, -7.12) * mm, "mid": v(15.67, -7.34) * mm, "end": v(15.57, -7.53) * mm});
            skLineSegment(sketch, "E161.MirrorCS", {"start": v(15.57, -7.53) * mm, "end": v(14.63, -8.86) * mm});
            skLineSegment(sketch, "E162.MirrorCS", {"start": v(14.5, -9.27) * mm, "end": v(14.5, -13.8) * mm});
            skArc(sketch, "E163.MirrorCS", {"start": v(14.5, -9.27) * mm, "mid": v(14.53, -9.06) * mm, "end": v(14.63, -8.86) * mm});
            skArc(sketch, "E164.MirrorCS", {"start": v(14.5, -13.8) * mm, "mid": v(14.3, -14.3) * mm, "end": v(13.8, -14.5) * mm});
            skLineSegment(sketch, "E165.MirrorCS", {"start": v(9.27, -14.5) * mm, "end": v(13.8, -14.5) * mm});
            skArc(sketch, "E166.MirrorCS", {"start": v(8.86, -14.63) * mm, "mid": v(9.06, -14.53) * mm, "end": v(9.27, -14.5) * mm});
            skLineSegment(sketch, "E167.MirrorCS", {"start": v(7.53, -15.57) * mm, "end": v(8.86, -14.63) * mm});
            skArc(sketch, "E168.MirrorCS", {"start": v(6.6, -15.7) * mm, "mid": v(6.1, -15.5) * mm, "end": v(5.9, -15) * mm});
            skLineSegment(sketch, "E169.MirrorCS", {"start": v(6.6, -15.7) * mm, "end": v(7.12, -15.7) * mm});
            skArc(sketch, "E170.MirrorCS", {"start": v(7.53, -15.57) * mm, "mid": v(7.34, -15.67) * mm, "end": v(7.12, -15.7) * mm});
            skLineSegment(sketch, "E171.1.0", {"start": v(16.65, -21.4) * mm, "end": v(21.63, -22.46) * mm});
            skArc(sketch, "E171.1.1", {"start": v(16.1, -20.7) * mm, "mid": v(16.26, -21.15) * mm, "end": v(16.65, -21.4) * mm});
            skLineSegment(sketch, "E171.1.2", {"start": v(16.1, -16.8) * mm, "end": v(16.1, -20.7) * mm});
            skArc(sketch, "E171.1.3", {"start": v(16.8, -16.1) * mm, "mid": v(16.3, -16.3) * mm, "end": v(16.1, -16.8) * mm});
            skLineSegment(sketch, "E171.1.4", {"start": v(16.8, -16.1) * mm, "end": v(20.7, -16.1) * mm});
            skArc(sketch, "E171.1.5", {"start": v(21.4, -16.65) * mm, "mid": v(21.15, -16.26) * mm, "end": v(20.7, -16.1) * mm});
            skLineSegment(sketch, "E171.1.6", {"start": v(21.4, -16.65) * mm, "end": v(22.46, -21.63) * mm});
            skArc(sketch, "E171.1.7", {"start": v(21.63, -22.46) * mm, "mid": v(22.27, -22.27) * mm, "end": v(22.46, -21.63) * mm});
            skLineSegment(sketch, "E171.2.0", {"start": v(21.4, 16.65) * mm, "end": v(22.46, 21.63) * mm});
            skArc(sketch, "E171.2.1", {"start": v(20.7, 16.1) * mm, "mid": v(21.15, 16.26) * mm, "end": v(21.4, 16.65) * mm});
            skLineSegment(sketch, "E171.2.2", {"start": v(16.8, 16.1) * mm, "end": v(20.7, 16.1) * mm});
            skArc(sketch, "E171.2.3", {"start": v(16.1, 16.8) * mm, "mid": v(16.3, 16.3) * mm, "end": v(16.8, 16.1) * mm});
            skLineSegment(sketch, "E171.2.4", {"start": v(16.1, 16.8) * mm, "end": v(16.1, 20.7) * mm});
            skArc(sketch, "E171.2.5", {"start": v(16.65, 21.4) * mm, "mid": v(16.26, 21.15) * mm, "end": v(16.1, 20.7) * mm});
            skLineSegment(sketch, "E171.2.6", {"start": v(16.65, 21.4) * mm, "end": v(21.63, 22.46) * mm});
            skArc(sketch, "E171.2.7", {"start": v(22.46, 21.63) * mm, "mid": v(22.27, 22.27) * mm, "end": v(21.63, 22.46) * mm});
            skLineSegment(sketch, "E171.3.0", {"start": v(-16.65, 21.4) * mm, "end": v(-21.63, 22.46) * mm});
            skArc(sketch, "E171.3.1", {"start": v(-16.1, 20.7) * mm, "mid": v(-16.26, 21.15) * mm, "end": v(-16.65, 21.4) * mm});
            skLineSegment(sketch, "E171.3.2", {"start": v(-16.1, 16.8) * mm, "end": v(-16.1, 20.7) * mm});
            skArc(sketch, "E171.3.3", {"start": v(-16.8, 16.1) * mm, "mid": v(-16.3, 16.3) * mm, "end": v(-16.1, 16.8) * mm});
            skLineSegment(sketch, "E171.3.4", {"start": v(-16.8, 16.1) * mm, "end": v(-20.7, 16.1) * mm});
            skArc(sketch, "E171.3.5", {"start": v(-21.4, 16.65) * mm, "mid": v(-21.15, 16.26) * mm, "end": v(-20.7, 16.1) * mm});
            skLineSegment(sketch, "E171.3.6", {"start": v(-21.4, 16.65) * mm, "end": v(-22.46, 21.63) * mm});
            skArc(sketch, "E171.3.7", {"start": v(-21.63, 22.46) * mm, "mid": v(-22.27, 22.27) * mm, "end": v(-22.46, 21.63) * mm});
            skArc(sketch, "E172.1.0", {"start": v(20.02, -14.5) * mm, "mid": v(20.57, -14.24) * mm, "end": v(20.7, -13.65) * mm});
            skLineSegment(sketch, "E172.1.1", {"start": v(20.02, -14.5) * mm, "end": v(16.8, -14.5) * mm});
            skArc(sketch, "E172.1.2", {"start": v(16.1, -13.8) * mm, "mid": v(16.3, -14.3) * mm, "end": v(16.8, -14.5) * mm});
            skLineSegment(sketch, "E172.1.3", {"start": v(16.1, -13.8) * mm, "end": v(16.1, -10.78) * mm});
            skArc(sketch, "E172.1.4", {"start": v(16.23, -10.37) * mm, "mid": v(16.13, -10.56) * mm, "end": v(16.1, -10.78) * mm});
            skLineSegment(sketch, "E172.1.5", {"start": v(16.23, -10.37) * mm, "end": v(17.17, -9.04) * mm});
            skArc(sketch, "E172.1.6", {"start": v(17.17, -9.04) * mm, "mid": v(17.27, -8.84) * mm, "end": v(17.3, -8.63) * mm});
            skLineSegment(sketch, "E172.1.7", {"start": v(17.3, -8.63) * mm, "end": v(17.3, -6.6) * mm});
            skArc(sketch, "E172.1.8", {"start": v(18, -5.9) * mm, "mid": v(17.5, -6.1) * mm, "end": v(17.3, -6.6) * mm});
            skLineSegment(sketch, "E172.1.9", {"start": v(18, -5.9) * mm, "end": v(18.84, -5.9) * mm});
            skArc(sketch, "E172.1.10", {"start": v(19.54, -6.53) * mm, "mid": v(19.31, -6.08) * mm, "end": v(18.84, -5.9) * mm});
            skArc(sketch, "E172.1.11", {"start": v(19.54, -6.53) * mm, "mid": v(20.02, -10.1) * mm, "end": v(20.7, -13.65) * mm});
            skArc(sketch, "E172.2.0", {"start": v(14.5, 20.02) * mm, "mid": v(14.24, 20.57) * mm, "end": v(13.65, 20.7) * mm});
            skLineSegment(sketch, "E172.2.1", {"start": v(14.5, 20.02) * mm, "end": v(14.5, 16.8) * mm});
            skArc(sketch, "E172.2.2", {"start": v(13.8, 16.1) * mm, "mid": v(14.3, 16.3) * mm, "end": v(14.5, 16.8) * mm});
            skLineSegment(sketch, "E172.2.3", {"start": v(13.8, 16.1) * mm, "end": v(10.78, 16.1) * mm});
            skArc(sketch, "E172.2.4", {"start": v(10.37, 16.23) * mm, "mid": v(10.56, 16.13) * mm, "end": v(10.78, 16.1) * mm});
            skLineSegment(sketch, "E172.2.5", {"start": v(10.37, 16.23) * mm, "end": v(9.04, 17.17) * mm});
            skArc(sketch, "E172.2.6", {"start": v(9.04, 17.17) * mm, "mid": v(8.84, 17.27) * mm, "end": v(8.63, 17.3) * mm});
            skLineSegment(sketch, "E172.2.7", {"start": v(8.63, 17.3) * mm, "end": v(6.6, 17.3) * mm});
            skArc(sketch, "E172.2.8", {"start": v(5.9, 18) * mm, "mid": v(6.1, 17.5) * mm, "end": v(6.6, 17.3) * mm});
            skLineSegment(sketch, "E172.2.9", {"start": v(5.9, 18) * mm, "end": v(5.9, 18.84) * mm});
            skArc(sketch, "E172.2.10", {"start": v(6.53, 19.54) * mm, "mid": v(6.08, 19.31) * mm, "end": v(5.9, 18.84) * mm});
            skArc(sketch, "E172.2.11", {"start": v(6.53, 19.54) * mm, "mid": v(10.1, 20.02) * mm, "end": v(13.65, 20.7) * mm});
            skArc(sketch, "E172.3.0", {"start": v(-20.02, 14.5) * mm, "mid": v(-20.57, 14.24) * mm, "end": v(-20.7, 13.65) * mm});
            skLineSegment(sketch, "E172.3.1", {"start": v(-20.02, 14.5) * mm, "end": v(-16.8, 14.5) * mm});
            skArc(sketch, "E172.3.2", {"start": v(-16.1, 13.8) * mm, "mid": v(-16.3, 14.3) * mm, "end": v(-16.8, 14.5) * mm});
            skLineSegment(sketch, "E172.3.3", {"start": v(-16.1, 13.8) * mm, "end": v(-16.1, 10.78) * mm});
            skArc(sketch, "E172.3.4", {"start": v(-16.23, 10.37) * mm, "mid": v(-16.13, 10.56) * mm, "end": v(-16.1, 10.78) * mm});
            skLineSegment(sketch, "E172.3.5", {"start": v(-16.23, 10.37) * mm, "end": v(-17.17, 9.04) * mm});
            skArc(sketch, "E172.3.6", {"start": v(-17.17, 9.04) * mm, "mid": v(-17.27, 8.84) * mm, "end": v(-17.3, 8.63) * mm});
            skLineSegment(sketch, "E172.3.7", {"start": v(-17.3, 8.63) * mm, "end": v(-17.3, 6.6) * mm});
            skArc(sketch, "E172.3.8", {"start": v(-18, 5.9) * mm, "mid": v(-17.5, 6.1) * mm, "end": v(-17.3, 6.6) * mm});
            skLineSegment(sketch, "E172.3.9", {"start": v(-18, 5.9) * mm, "end": v(-18.84, 5.9) * mm});
            skArc(sketch, "E172.3.10", {"start": v(-19.54, 6.53) * mm, "mid": v(-19.31, 6.08) * mm, "end": v(-18.84, 5.9) * mm});
            skArc(sketch, "E172.3.11", {"start": v(-19.54, 6.53) * mm, "mid": v(-20.02, 10.1) * mm, "end": v(-20.7, 13.65) * mm});
            skPoint(sketch, "E173.endSnap0", {"position": v(5.9, 0) * mm});
            skLineSegment(sketch, "E174", {"start": v(0, 0) * mm, "end": v(-5.1, 0) * mm, "construction": true});
            skArc(sketch, "E175.1.0", {"start": v(18, 5.9) * mm, "mid": v(17.5, 6.1) * mm, "end": v(17.3, 6.6) * mm});
            skLineSegment(sketch, "E175.1.1", {"start": v(18, 5.9) * mm, "end": v(18.84, 5.9) * mm});
            skArc(sketch, "E175.1.2", {"start": v(19.54, 6.53) * mm, "mid": v(19.31, 6.08) * mm, "end": v(18.84, 5.9) * mm});
            skArc(sketch, "E175.1.3", {"start": v(19.54, 6.53) * mm, "mid": v(20.02, 10.1) * mm, "end": v(20.7, 13.65) * mm});
            skLineSegment(sketch, "E175.1.4", {"start": v(17.3, 8.63) * mm, "end": v(17.3, 6.6) * mm});
            skArc(sketch, "E175.1.5", {"start": v(17.17, 9.04) * mm, "mid": v(17.27, 8.84) * mm, "end": v(17.3, 8.63) * mm});
            skLineSegment(sketch, "E175.1.6", {"start": v(16.23, 10.37) * mm, "end": v(17.17, 9.04) * mm});
            skArc(sketch, "E175.1.7", {"start": v(16.23, 10.37) * mm, "mid": v(16.13, 10.56) * mm, "end": v(16.1, 10.78) * mm});
            skLineSegment(sketch, "E175.1.8", {"start": v(16.1, 13.8) * mm, "end": v(16.1, 10.78) * mm});
            skArc(sketch, "E175.1.9", {"start": v(16.1, 13.8) * mm, "mid": v(16.3, 14.3) * mm, "end": v(16.8, 14.5) * mm});
            skLineSegment(sketch, "E175.1.10", {"start": v(20.02, 14.5) * mm, "end": v(16.8, 14.5) * mm});
            skArc(sketch, "E175.1.11", {"start": v(20.02, 14.5) * mm, "mid": v(20.57, 14.24) * mm, "end": v(20.7, 13.65) * mm});
            skArc(sketch, "E175.2.0", {"start": v(-5.9, 18) * mm, "mid": v(-6.1, 17.5) * mm, "end": v(-6.6, 17.3) * mm});
            skLineSegment(sketch, "E175.2.1", {"start": v(-5.9, 18) * mm, "end": v(-5.9, 18.84) * mm});
            skArc(sketch, "E175.2.2", {"start": v(-6.53, 19.54) * mm, "mid": v(-6.08, 19.31) * mm, "end": v(-5.9, 18.84) * mm});
            skArc(sketch, "E175.2.3", {"start": v(-6.53, 19.54) * mm, "mid": v(-10.1, 20.02) * mm, "end": v(-13.65, 20.7) * mm});
            skLineSegment(sketch, "E175.2.4", {"start": v(-8.63, 17.3) * mm, "end": v(-6.6, 17.3) * mm});
            skArc(sketch, "E175.2.5", {"start": v(-9.04, 17.17) * mm, "mid": v(-8.84, 17.27) * mm, "end": v(-8.63, 17.3) * mm});
            skLineSegment(sketch, "E175.2.6", {"start": v(-10.37, 16.23) * mm, "end": v(-9.04, 17.17) * mm});
            skArc(sketch, "E175.2.7", {"start": v(-10.37, 16.23) * mm, "mid": v(-10.56, 16.13) * mm, "end": v(-10.78, 16.1) * mm});
            skLineSegment(sketch, "E175.2.8", {"start": v(-13.8, 16.1) * mm, "end": v(-10.78, 16.1) * mm});
            skArc(sketch, "E175.2.9", {"start": v(-13.8, 16.1) * mm, "mid": v(-14.3, 16.3) * mm, "end": v(-14.5, 16.8) * mm});
            skLineSegment(sketch, "E175.2.10", {"start": v(-14.5, 20.02) * mm, "end": v(-14.5, 16.8) * mm});
            skArc(sketch, "E175.2.11", {"start": v(-14.5, 20.02) * mm, "mid": v(-14.24, 20.57) * mm, "end": v(-13.65, 20.7) * mm});
            skArc(sketch, "E175.3.0", {"start": v(-18, -5.9) * mm, "mid": v(-17.5, -6.1) * mm, "end": v(-17.3, -6.6) * mm});
            skLineSegment(sketch, "E175.3.1", {"start": v(-18, -5.9) * mm, "end": v(-18.84, -5.9) * mm});
            skArc(sketch, "E175.3.2", {"start": v(-19.54, -6.53) * mm, "mid": v(-19.31, -6.08) * mm, "end": v(-18.84, -5.9) * mm});
            skArc(sketch, "E175.3.3", {"start": v(-19.54, -6.53) * mm, "mid": v(-20.02, -10.1) * mm, "end": v(-20.7, -13.65) * mm});
            skLineSegment(sketch, "E175.3.4", {"start": v(-17.3, -8.63) * mm, "end": v(-17.3, -6.6) * mm});
            skArc(sketch, "E175.3.5", {"start": v(-17.17, -9.04) * mm, "mid": v(-17.27, -8.84) * mm, "end": v(-17.3, -8.63) * mm});
            skLineSegment(sketch, "E175.3.6", {"start": v(-16.23, -10.37) * mm, "end": v(-17.17, -9.04) * mm});
            skArc(sketch, "E175.3.7", {"start": v(-16.23, -10.37) * mm, "mid": v(-16.13, -10.56) * mm, "end": v(-16.1, -10.78) * mm});
            skLineSegment(sketch, "E175.3.8", {"start": v(-16.1, -13.8) * mm, "end": v(-16.1, -10.78) * mm});
            skArc(sketch, "E175.3.9", {"start": v(-16.1, -13.8) * mm, "mid": v(-16.3, -14.3) * mm, "end": v(-16.8, -14.5) * mm});
            skLineSegment(sketch, "E175.3.10", {"start": v(-20.02, -14.5) * mm, "end": v(-16.8, -14.5) * mm});
            skArc(sketch, "E175.3.11", {"start": v(-20.02, -14.5) * mm, "mid": v(-20.57, -14.24) * mm, "end": v(-20.7, -13.65) * mm});
            skLineSegment(sketch, "E176.MirrorCS", {"start": v(5.9, 6.6) * mm, "end": v(5.9, 15) * mm});
            skArc(sketch, "E177.MirrorCS", {"start": v(6.6, 5.9) * mm, "mid": v(6.1, 6.1) * mm, "end": v(5.9, 6.6) * mm});
            skLineSegment(sketch, "E178.MirrorCS", {"start": v(6.6, 5.9) * mm, "end": v(15, 5.9) * mm});
            skArc(sketch, "E179.MirrorCS", {"start": v(15.7, 6.6) * mm, "mid": v(15.5, 6.1) * mm, "end": v(15, 5.9) * mm});
            skLineSegment(sketch, "E180.MirrorCS", {"start": v(15.7, 6.6) * mm, "end": v(15.7, 7.12) * mm});
            skArc(sketch, "E181.MirrorCS", {"start": v(15.57, 7.53) * mm, "mid": v(15.67, 7.34) * mm, "end": v(15.7, 7.12) * mm});
            skLineSegment(sketch, "E182.MirrorCS", {"start": v(15.57, 7.53) * mm, "end": v(14.63, 8.86) * mm});
            skArc(sketch, "E183.MirrorCS", {"start": v(14.63, 8.86) * mm, "mid": v(14.53, 9.06) * mm, "end": v(14.5, 9.27) * mm});
            skLineSegment(sketch, "E184.MirrorCS", {"start": v(14.5, 9.27) * mm, "end": v(14.5, 13.8) * mm});
            skArc(sketch, "E185.MirrorCS", {"start": v(13.8, 14.5) * mm, "mid": v(14.3, 14.3) * mm, "end": v(14.5, 13.8) * mm});
            skLineSegment(sketch, "E186.MirrorCS", {"start": v(9.27, 14.5) * mm, "end": v(13.8, 14.5) * mm});
            skArc(sketch, "E187.MirrorCS", {"start": v(9.27, 14.5) * mm, "mid": v(9.06, 14.53) * mm, "end": v(8.86, 14.63) * mm});
            skLineSegment(sketch, "E188.MirrorCS", {"start": v(7.53, 15.57) * mm, "end": v(8.86, 14.63) * mm});
            skArc(sketch, "E189.MirrorCS", {"start": v(7.12, 15.7) * mm, "mid": v(7.34, 15.67) * mm, "end": v(7.53, 15.57) * mm});
            skLineSegment(sketch, "E190.MirrorCS", {"start": v(6.6, 15.7) * mm, "end": v(7.12, 15.7) * mm});
            skArc(sketch, "E191.MirrorCS", {"start": v(5.9, 15) * mm, "mid": v(6.1, 15.5) * mm, "end": v(6.6, 15.7) * mm});
            skArc(sketch, "E192.MirrorCS", {"start": v(-9.27, 14.5) * mm, "mid": v(-9.06, 14.53) * mm, "end": v(-8.86, 14.63) * mm});
            skLineSegment(sketch, "E193.MirrorCS", {"start": v(-15.7, 6.6) * mm, "end": v(-15.7, 7.12) * mm});
            skArc(sketch, "E194.MirrorCS", {"start": v(-7.12, 15.7) * mm, "mid": v(-7.34, 15.67) * mm, "end": v(-7.53, 15.57) * mm});
            skArc(sketch, "E195.MirrorCS", {"start": v(-14.63, 8.86) * mm, "mid": v(-14.53, 9.06) * mm, "end": v(-14.5, 9.27) * mm});
            skLineSegment(sketch, "E196.MirrorCS", {"start": v(-6.6, 15.7) * mm, "end": v(-7.12, 15.7) * mm});
            skArc(sketch, "E197.MirrorCS", {"start": v(-15.57, 7.53) * mm, "mid": v(-15.67, 7.34) * mm, "end": v(-15.7, 7.12) * mm});
            skLineSegment(sketch, "E198.MirrorCS", {"start": v(-7.53, 15.57) * mm, "end": v(-8.86, 14.63) * mm});
            skArc(sketch, "E199.MirrorCS", {"start": v(-5.9, 15) * mm, "mid": v(-6.1, 15.5) * mm, "end": v(-6.6, 15.7) * mm});
            skLineSegment(sketch, "E200.MirrorCS", {"start": v(-15.57, 7.53) * mm, "end": v(-14.63, 8.86) * mm});
            skLineSegment(sketch, "E201.MirrorCS", {"start": v(-5.9, 6.6) * mm, "end": v(-5.9, 15) * mm});
            skLineSegment(sketch, "E202.MirrorCS", {"start": v(-14.5, 9.27) * mm, "end": v(-14.5, 13.8) * mm});
            skArc(sketch, "E203.MirrorCS", {"start": v(-6.6, 5.9) * mm, "mid": v(-6.1, 6.1) * mm, "end": v(-5.9, 6.6) * mm});
            skLineSegment(sketch, "E204.MirrorCS", {"start": v(-6.6, 5.9) * mm, "end": v(-15, 5.9) * mm});
            skLineSegment(sketch, "E205.MirrorCS", {"start": v(-9.27, 14.5) * mm, "end": v(-13.8, 14.5) * mm});
            skArc(sketch, "E206.MirrorCS", {"start": v(-13.8, 14.5) * mm, "mid": v(-14.3, 14.3) * mm, "end": v(-14.5, 13.8) * mm});
            skArc(sketch, "E207.MirrorCS", {"start": v(-15.7, 6.6) * mm, "mid": v(-15.5, 6.1) * mm, "end": v(-15, 5.9) * mm});
            skSolve(sketch);
        }
        {
            var Q0;
            Q0 = qSketchRegion(id + "F0", true);
            extrude(context, id + "F1", {"entities" : qUnion([Q0]), "depth" : 0.5 * mm});
        }
    });
